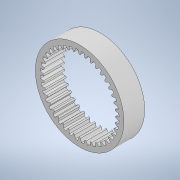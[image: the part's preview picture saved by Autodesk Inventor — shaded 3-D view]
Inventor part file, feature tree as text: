
AUTODESK INVENTOR PART (.ipt)
format: ipt  version: 2022 (Build 260153000, 153)  size: 409,088 bytes
history: native  units: in
note: dims shown in document units (in); Inventor stores cm internally (conversion verified against a paired STEP export)
features: sketch x6, extrude x5, pattern_circular x1, other x1, fillet x1, chamfer x1
ambient origin geometry x8: Origin, YZ Plane, XZ Plane, XY Plane, X Axis, Y Axis, Z Axis, Center Point
bodies: Solid1 (feature_tree)
feature tree (15):
  extrude  "Extrusion1"  Depth=0.7559in
  pattern_circular  "Circular Pattern1"  Count=4  [1 undecoded]
  extrude  "Extrusion6"  Depth=1.9685in
  sketch  "Sketch7"  dims[d3=0.025in]
  other  "Work Axis1"
  extrude  "Extrusion7"  Depth=2.1654in
  extrude  "Extrusion8"  Depth=1.0in TaperAngle=0.0deg
  extrude  "Extrusion9"  Depth=0.6693in
  fillet  "Fillet1"  Radius=0.315in
  chamfer  "Chamfer3"  Distance=1.8504in
  sketch  "Sketch1"  dims[d0=0.075in d1=0.7559in]
  sketch  "Sketch6"  dims[d2=0.7559in]
  sketch  "Sketch8"  dims[d10=0.4331in d11=0.0in]
  sketch  "Sketch9"  dims[d12=0.0375in d13=1.5748in]
  sketch  "Sketch10"  dims[d14=1.85in d33=1.9685in d34=2.1654in d35=1.0in d36=0.0in d37=0.6693in d38=0.315in d39=0.0in d40=1.8504in d41=0.315in d42=0.0in d43=0.9843in d44=0.2362in d45=0.1181in d46=0.1575in d47=0.0in d51=0.125in d52=0.0394in d53=0.0394in d54=0.125in d55=45.0deg d60=15.748in d61=360.0deg]
note: 1 required parameter value undecoded (feature->parameter linkage not recoverable at this tier; creation-order binding heuristic only, values carry confidence <= 0.55)
